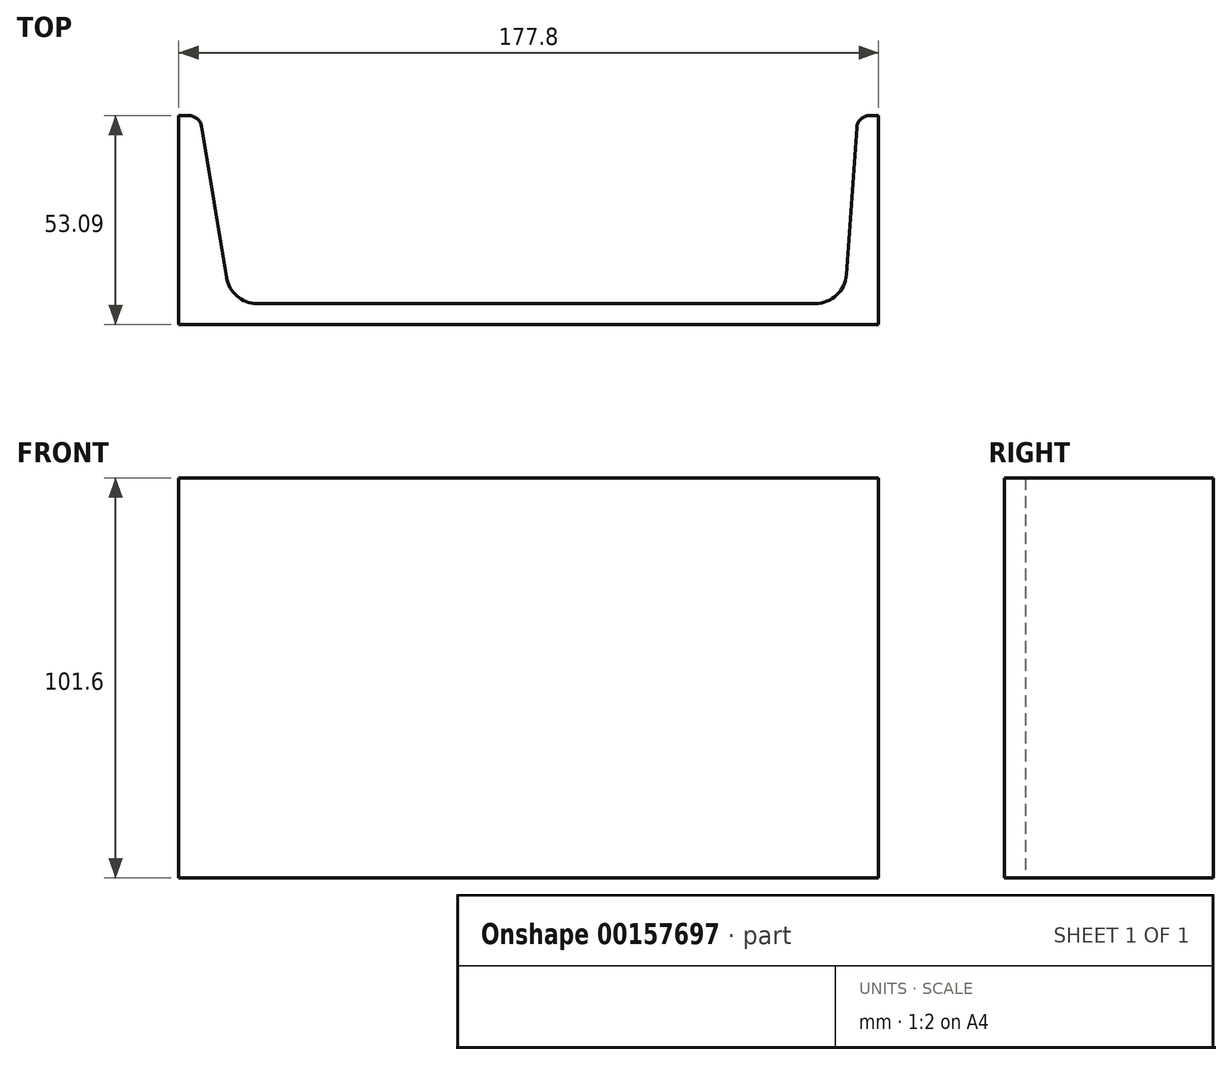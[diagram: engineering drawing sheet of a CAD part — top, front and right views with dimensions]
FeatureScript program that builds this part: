
annotation { "Feature Type Name" : "Feature", "Feature Type Description" : "" }
export const myFeature = defineFeature(function(context is Context, id is Id, definition is map)
    precondition{}
    {
        {
            var Q0;
            Q0=qCreatedBy(makeId("Top.planeOp"),FACE);
            var sketch = newSketch(context, id + "F0", { "sketchPlane" : qUnion([Q0])});
            skLineSegment(sketch, "E0", {"start": v(88.61, -0.02) * mm, "end": v(-89.19, -0.02) * mm});
            skLineSegment(sketch, "E1", {"start": v(-89.19, -0.02) * mm, "end": v(-89.19, 53.07) * mm});
            skLineSegment(sketch, "E2", {"start": v(88.61, -0.02) * mm, "end": v(88.61, 53.07) * mm});
            skLineSegment(sketch, "E3", {"start": v(88.61, 53.07) * mm, "end": v(86.36, 53.07) * mm});
            skLineSegment(sketch, "E4", {"start": v(-89.19, 53.07) * mm, "end": v(-86.65, 53.07) * mm});
            skLineSegment(sketch, "E5", {"start": v(-69.3, 5.33) * mm, "end": v(72.6, 5.33) * mm});
            skLineSegment(sketch, "E6", {"start": v(-83.4, 50.3) * mm, "end": v(-77.07, 11.93) * mm});
            skLineSegment(sketch, "E7", {"start": v(83.06, 50) * mm, "end": v(80.46, 12.66) * mm});
            skPoint(sketch, "E8.visualSharp", {"position": v(-83.85, 53.07) * mm});
            skArc(sketch, "E8.filletArc", {"start": v(-83.4, 50.3) * mm, "mid": v(-84.52, 52.28) * mm, "end": v(-86.65, 53.07) * mm});
            skPoint(sketch, "E9.visualSharp", {"position": v(83.28, 53.07) * mm});
            skArc(sketch, "E9.filletArc", {"start": v(86.36, 53.07) * mm, "mid": v(84.1, 52.18) * mm, "end": v(83.06, 50) * mm});
            skArc(sketch, "E10.filletArc", {"start": v(72.6, 5.33) * mm, "mid": v(77.97, 7.45) * mm, "end": v(80.46, 12.66) * mm});
            skArc(sketch, "E11.filletArc", {"start": v(-77.07, 11.93) * mm, "mid": v(-74.4, 7.2) * mm, "end": v(-69.3, 5.33) * mm});
            skSolve(sketch);
        }
        {
            var Q0;
            Q0=makeQuery(id+"F0.imprint","IMPRINT",FACE,{"disambiguationData":[TD([[makeQuery(id+"F0.imprint","IMPRINT",EDGE,{"derivedFrom":sQuery(id+"F0.wireOp",EDGE,"E0")}),-1.0]])]});
            extrude(context, id + "F1", {"entities" : qUnion([Q0]), "depth" : 101.6 * mm});
        }
    });
